# Revit family: IEK_РозеткаТелевизионная_ОткрытойУстановки_1-местная_ОКТАВА
name_source: partatom
category: Устройства связи
units: mm (PartAtom-declared; Revit-internal decimal feet)

## family parameters
Всегда вертикально = Да
На основе рабочей плоскости = Нет
Общий = Нет
При загрузке вырезать с полостями = Нет
Размер круглого соединителя = Использовать диаметр
Сохранять ориентацию аннотаций = Да
Тип детали = Нормальный
Точка расчета площади = Нет

## types (2) — shared parameters
ADSK_URL страницы изделия = https://www.iek.ru
ADSK_Версия Revit = 2019
ADSK_Версия семейства = 1.0
ADSK_Группирование = III ЭЛЕКТРОУСТАНОВОЧНЫЕ И ЭЛЕКТРОМОНТАЖНЫЕ ИЗДЕЛИЯ
ADSK_Единица измерения = шт
ADSK_Завод-изготовитель = IEK
ADSK_Марка = ОКТАВА
ADSK_Материал наименование = Пластик
IEK_URL = https://www.iek.ru
IEK_Описание = Универсальный дизайн серии открытой установки "ОКТАВА" позволяет устанавливать изделия в квартирах, загородных домах, офисных и производственных помещениях.
KSI_CMa_Строительные материалы = 01.7.14.03
Высота = 61 мм
Глубина = 35 мм
Изготовитель = IEK
Тип монтажа = Поверхность монтажа (открытая установка)
Тип соединителя или разъема = TV-SAT
Ширина = 61 мм

## per-type parameters (varying)
| type | ADSK_Код изделия | ADSK_Масса | ADSK_Материал | ADSK_Наименование | IEK_Цена за единицу |
| РТВ20-ОКм | EAO10-K33-DC | 0.051 | Цвет кремовый | Розетка 1-местная для открытой установки телевизионная РТВ20-ОКм ОКТАВА кремовый IEK | 124.86 |
| РТВ20-ОС | EAO10-K03-DC | 0.050926 | Цвет сосна | Розетка 1-местная для открытой установки телевизионная РТВ20-ОС ОКТАВА сосна IEK | 165.88 |
